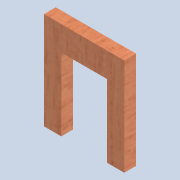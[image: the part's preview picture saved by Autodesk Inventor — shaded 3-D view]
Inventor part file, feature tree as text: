
AUTODESK INVENTOR PART (.ipt)
format: ipt  version: 2020 (Build 240168000, 168)  size: 128,512 bytes
history: native  units: mm
features: reference x4, other x3, extrude x2, sketch x2
ambient origin geometry x8: Origin, YZ Plane, XZ Plane, XY Plane, X Axis, Y Axis, Z Axis, Center Point
bodies: Solid1 (feature_tree)
feature tree (11):
  extrude  "Extrusion1"  Depth=66.0mm
  extrude  "Extrusion2"  TaperAngle=0.0deg  [1 undecoded]
  sketch  "Sketch1"  dims[d0=54.5mm d1=66.0mm]
  sketch  "Sketch2"  dims[d2=8.0mm d3=0.0mm d6=0.0mm d7=0.0mm d29=2.0mm d30=2.0mm d32=2.0mm]
  reference  "Reference8"
  reference  "Reference9"
  reference  "Reference10"
  reference  "Reference11"
  parser-record x1  (decoder bookkeeping rows leaked as tree rows — omitted from the tree; the rows remain in map.json)
  other  "0005-00-00 Ansamblu_General.iam"
  other  "Inlet Module Plug Fuse Switch Male Power Socket 10A 250V 3 Pin IEC320 C14.ipt:82"
note: 1 required parameter value undecoded (feature->parameter linkage not recoverable at this tier; creation-order binding heuristic only, values carry confidence <= 0.55)
note: 1 file-system path scrubbed to <path> (originals preserved in map.json)
